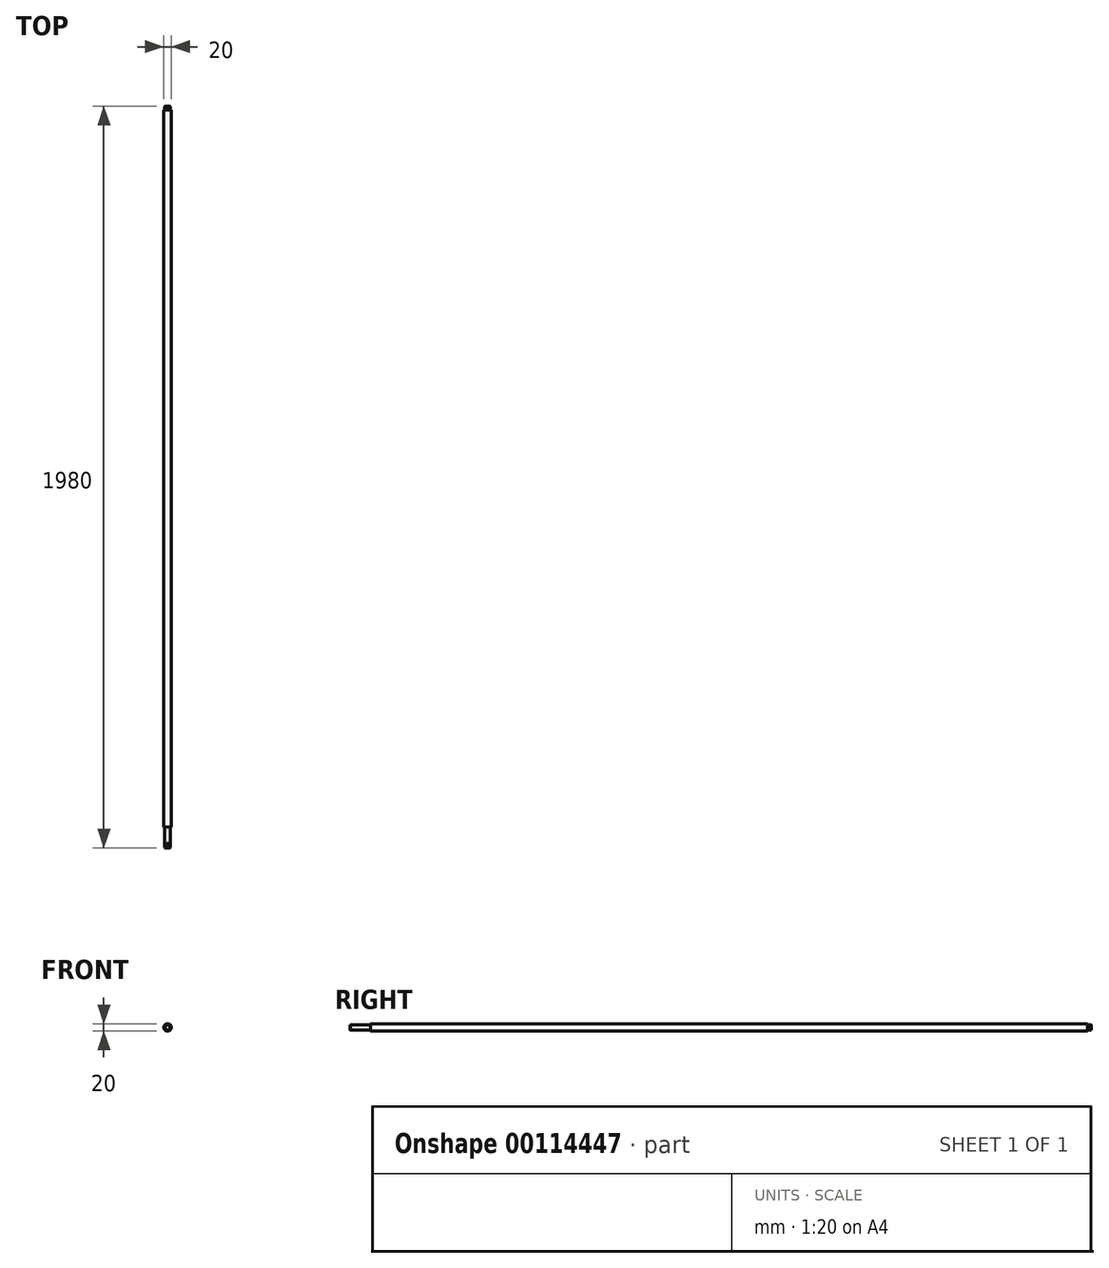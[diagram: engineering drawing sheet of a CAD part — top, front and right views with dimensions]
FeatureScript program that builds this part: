
annotation { "Feature Type Name" : "Feature", "Feature Type Description" : "" }
export const myFeature = defineFeature(function(context is Context, id is Id, definition is map)
    precondition{}
    {
        {
            var Q0;
            Q0=qCreatedBy(makeId("Front.planeOp"),FACE);
            var sketch = newSketch(context, id + "F0", { "sketchPlane" : qUnion([Q0])});
            skCircle(sketch, "E0", {"center": v(0, 0) * mm, "radius": 10 * mm});
            skSolve(sketch);
        }
        {
            var Q0;
            Q0=makeQuery(id+"F0.imprint","IMPRINT",FACE,{"disambiguationData":[TD([[makeQuery(id+"F0.imprint","IMPRINT",EDGE,{"derivedFrom":sQuery(id+"F0.wireOp",EDGE,"E0")}),1.0]])]});
            extrude(context, id + "F1", {"entities" : qUnion([Q0]), "depth" : 1915 * mm});
        }
        {
            var Q0;
            Q0=makeQuery(id+"F1.opExtrude","CAP_FACE",FACE,{"disambiguationData":[OSD([sQuery(id+"F0.wireOp",EDGE,"E0")])],"isStart":false});
            var sketch = newSketch(context, id + "F2", { "sketchPlane" : qUnion([Q0])});
            skCircle(sketch, "E1", {"center": v(0, 0) * mm, "radius": 7.5 * mm});
            skSolve(sketch);
        }
        {
            var Q0;
            Q0 = qSketchRegion(id + "F2", true);
            extrude(context, id + "F3", {"entities" : qUnion([Q0]), "operationType" : NewBodyOperationType.ADD, "depth" : 55 * mm});
        }
        {
            var Q0;
            Q0=makeQuery(id+"F1.opExtrude","CAP_FACE",FACE,{"disambiguationData":[OSD([sQuery(id+"F0.wireOp",EDGE,"E0")])],"isStart":true});
            var sketch = newSketch(context, id + "F4", { "sketchPlane" : qUnion([Q0])});
            skCircle(sketch, "E2", {"center": v(0, 0) * mm, "radius": 7.5 * mm});
            skSolve(sketch);
        }
        {
            var Q0;
            Q0 = qSketchRegion(id + "F4", true);
            extrude(context, id + "F5", {"entities" : qUnion([Q0]), "operationType" : NewBodyOperationType.ADD, "depth" : 10 * mm});
        }
        {
            var Q0;
            Q0=qCreatedBy(makeId("Top.planeOp"),FACE);
            cPlane(context, id + "F6", {"entities" : qUnion([Q0]), "cplaneType" : CPlaneType.OFFSET, "offset" : 7.5 * mm, "width" : 150 * mm, "height" : 150 * mm});
        }
        {
            var Q0;
            Q0=qCreatedBy(id+"F6.planeOp",FACE);
            var sketch = newSketch(context, id + "F7", { "sketchPlane" : qUnion([Q0])});
            skArc(sketch, "E3", {"start": v(2, -1960.1) * mm, "mid": v(0, -1958) * mm, "end": v(-2, -1960.1) * mm});
            skArc(sketch, "E4", {"start": v(-2, -1965.9) * mm, "mid": v(0, -1968) * mm, "end": v(2, -1965.9) * mm});
            skLineSegment(sketch, "E5", {"start": v(-2, -1960.1) * mm, "end": v(-2, -1966.1) * mm});
            skLineSegment(sketch, "E6", {"start": v(2, -1960.1) * mm, "end": v(2, -1966.1) * mm});
            skSolve(sketch);
        }
        {
            var Q0;
            Q0 = qSketchRegion(id + "F7", true);
            extrude(context, id + "F8", {"entities" : qUnion([Q0]), "operationType" : NewBodyOperationType.REMOVE, "oppositeDirection" : true, "depth" : 2 * mm});
        }
        {
            var Q0;
            Q0=makeQuery(id+"F3.opExtrude","CAP_EDGE",EDGE,{"disambiguationData":[OSD([sQuery(id+"F2.wireOp",EDGE,"E1")])],"isStart":false});
            var Q1;
            Q1=makeQuery(id+"F5.opExtrude","CAP_EDGE",EDGE,{"disambiguationData":[OSD([sQuery(id+"F4.wireOp",EDGE,"E2")])],"isStart":false});
            chamfer(context, id + "F9", {"entities" : qUnion([Q0, Q1]), "width" : 1 * mm, "tangentPropagation" : true});
        }
    });
